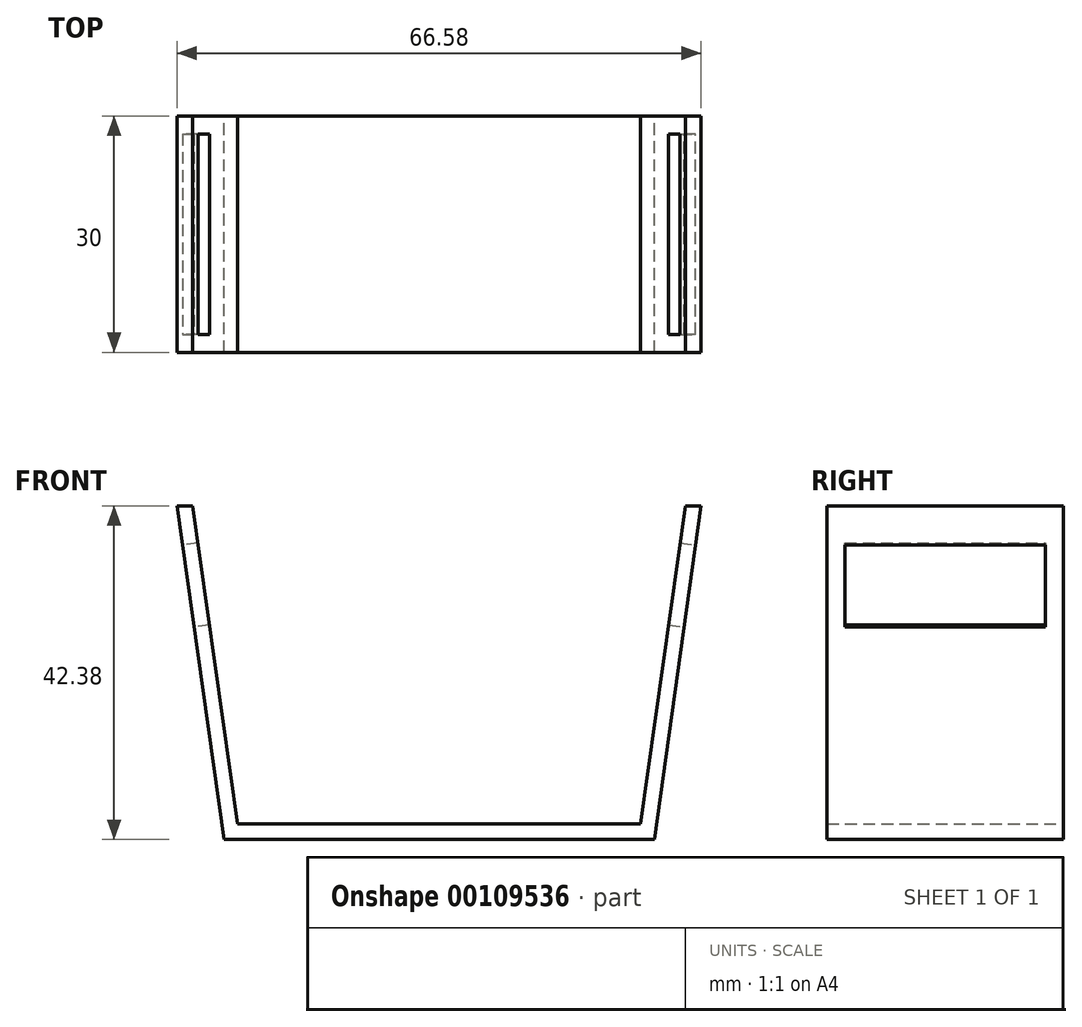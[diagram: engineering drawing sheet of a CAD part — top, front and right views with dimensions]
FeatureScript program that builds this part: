
annotation { "Feature Type Name" : "Feature", "Feature Type Description" : "" }
export const myFeature = defineFeature(function(context is Context, id is Id, definition is map)
    precondition{}
    {
        {
            var Q0;
            Q0=qCreatedBy(makeId("Front.planeOp"),FACE);
            var sketch = newSketch(context, id + "F0", { "sketchPlane" : qUnion([Q0])});
            skLineSegment(sketch, "E0", {"start": v(0, 0) * mm, "end": v(0, -5.67) * mm, "construction": true});
            skLineSegment(sketch, "E1", {"start": v(0, -5.67) * mm, "end": v(34.5, -5.67) * mm, "construction": true});
            skLineSegment(sketch, "E2", {"start": v(34.5, -5.67) * mm, "end": v(34.5, 0) * mm, "construction": true});
            skLineSegment(sketch, "E3.2", {"start": v(0, 2) * mm, "end": v(25.6, 2) * mm});
            skLineSegment(sketch, "E4.MirrorCS", {"start": v(-34.5, -5.67) * mm, "end": v(-34.5, 0) * mm, "construction": true});
            skLineSegment(sketch, "E5.MirrorCS", {"start": v(0, -5.67) * mm, "end": v(-34.5, -5.67) * mm, "construction": true});
            skLineSegment(sketch, "E6", {"start": v(31.27, 42.38) * mm, "end": v(25.6, 2) * mm});
            skLineSegment(sketch, "E7", {"start": v(27.34, 0) * mm, "end": v(33.29, 42.33) * mm});
            skLineSegment(sketch, "E8", {"start": v(31.27, 42.38) * mm, "end": v(33.29, 42.33) * mm});
            skLineSegment(sketch, "E9.MirrorCS", {"start": v(-31.27, 42.38) * mm, "end": v(-33.29, 42.33) * mm});
            skLineSegment(sketch, "E10.MirrorCS", {"start": v(-31.27, 42.38) * mm, "end": v(-25.6, 2) * mm});
            skLineSegment(sketch, "E11.MirrorCS", {"start": v(-27.34, 0) * mm, "end": v(-33.29, 42.33) * mm});
            skLineSegment(sketch, "E12.MirrorCS", {"start": v(0, 0) * mm, "end": v(-27.34, 0) * mm});
            skLineSegment(sketch, "E13.MirrorCS", {"start": v(0, 2) * mm, "end": v(-25.6, 2) * mm});
            skLineSegment(sketch, "E14", {"start": v(0, 0) * mm, "end": v(27.34, 0) * mm});
            skSolve(sketch);
        }
        {
            var Q0;
            Q0=qSketchRegion(id+"F0",true);
            extrude(context, id + "F1", {"entities" : qUnion([Q0]), "depth" : 30 * mm});
        }
        {
            var Q0;
            Q0=makeQuery(id+"F1.opExtrude","SWEPT_FACE",FACE,{"disambiguationData":[OSD([sQuery(id+"F0.wireOp",EDGE,"E7")])]});
            var sketch = newSketch(context, id + "F2", { "sketchPlane" : qUnion([Q0])});
            skLineSegment(sketch, "E15", {"start": v(-30, 46.55) * mm, "end": v(-30, 41.55) * mm, "construction": true});
            skLineSegment(sketch, "E16", {"start": v(-30, 41.55) * mm, "end": v(-30, 31.05) * mm, "construction": true});
            skLineSegment(sketch, "E17", {"start": v(-30, 46.55) * mm, "end": v(-27.75, 46.55) * mm, "construction": true});
            skLineSegment(sketch, "E18", {"start": v(0, 46.55) * mm, "end": v(-2.25, 46.55) * mm, "construction": true});
            skLineSegment(sketch, "E19", {"start": v(-27.75, 41.55) * mm, "end": v(-2.25, 41.55) * mm});
            skLineSegment(sketch, "E20", {"start": v(-27.75, 41.55) * mm, "end": v(-27.75, 31.05) * mm});
            skLineSegment(sketch, "E21", {"start": v(-2.25, 41.55) * mm, "end": v(-2.25, 31.05) * mm});
            skLineSegment(sketch, "E22", {"start": v(-27.75, 31.05) * mm, "end": v(-2.25, 31.05) * mm});
            skSolve(sketch);
        }
        {
            var Q0;
            Q0=qSketchRegion(id+"F2",true);
            extrude(context, id + "F3", {"entities" : qUnion([Q0]), "operationType" : NewBodyOperationType.REMOVE, "oppositeDirection" : true, "depth" : 5 * mm});
        }
        {
            var Q0;
            Q0=makeQuery(id+"F1.opExtrude","SWEPT_FACE",FACE,{"disambiguationData":[OSD([sQuery(id+"F0.wireOp",EDGE,"E11.MirrorCS")])]});
            var sketch = newSketch(context, id + "F4", { "sketchPlane" : qUnion([Q0])});
            skLineSegment(sketch, "E23", {"start": v(0, 46.55) * mm, "end": v(0, 41.55) * mm, "construction": true});
            skLineSegment(sketch, "E24", {"start": v(0, 41.55) * mm, "end": v(0, 31.05) * mm, "construction": true});
            skLineSegment(sketch, "E25", {"start": v(30, 46.55) * mm, "end": v(27.75, 46.55) * mm, "construction": true});
            skLineSegment(sketch, "E26", {"start": v(2.25, 41.55) * mm, "end": v(27.75, 41.55) * mm});
            skLineSegment(sketch, "E27", {"start": v(27.75, 41.55) * mm, "end": v(27.75, 31.05) * mm});
            skLineSegment(sketch, "E28", {"start": v(2.25, 31.05) * mm, "end": v(27.75, 31.05) * mm});
            skLineSegment(sketch, "E29", {"start": v(0, 46.55) * mm, "end": v(2.25, 46.55) * mm, "construction": true});
            skLineSegment(sketch, "E30", {"start": v(2.25, 41.55) * mm, "end": v(2.25, 31.05) * mm});
            skSolve(sketch);
        }
        {
            var Q0;
            Q0=qSketchRegion(id+"F4",true);
            extrude(context, id + "F5", {"entities" : qUnion([Q0]), "operationType" : NewBodyOperationType.REMOVE, "oppositeDirection" : true, "depth" : 5 * mm});
        }
    });
